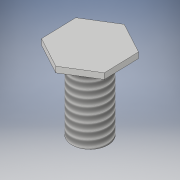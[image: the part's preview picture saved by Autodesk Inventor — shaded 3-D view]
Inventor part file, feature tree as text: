
AUTODESK INVENTOR PART (.ipt)
format: ipt  version: 2017 (Build 210142000, 142)  size: 111,616 bytes
history: native  units: in
note: dims shown in document units (in); Inventor stores cm internally (conversion verified against a paired STEP export)
features: extrude x2, sketch x2, thread x1
ambient origin geometry x8: Origin, YZ Plane, XZ Plane, XY Plane, X Axis, Y Axis, Z Axis, Center Point
bodies: Solid1 (feature_tree)
feature tree (5):
  extrude  "Extrusion1"  Depth=0.25in
  thread  "Thread1"  [1 undecoded]
  extrude  "Extrusion3"  Depth=0.02in TaperAngle=0.0deg
  sketch  "Sketch1"  dims[d0=0.5in d1=0.125in d2=0.25in d3=0.0in]
  sketch  "Sketch3"  dims[d7=1.0in d8=0.0in d11=0.02in d12=0.0in]
note: 1 required parameter value undecoded (feature->parameter linkage not recoverable at this tier; creation-order binding heuristic only, values carry confidence <= 0.55)
